# Revit family: Reece_Tap_Mizu_Bloc_Bath Outlet_160 mm
name_source: partatom
category: Plumbing Fixtures
revit_build: Autodesk Revit 2018 (Build: 20190510_1515(x64)
units: mm (PartAtom-declared; Revit-internal decimal feet)

## family parameters
Cut with Voids When Loaded = No
Host = Face
Part Type = Normal
Room Calculation Point = Yes
Round Connector Dimension = Use Diameter
Shared = Yes

## types (1)
- Chrome
    CWFU = 0
    Default Elevation = 1000 mm  [stored 3.28084 ft]
    Description = Mizu Bloc Bath Outlet 160mm Chrome
    Disclaimer = THIS FILE IS THE PROPERTY OF THE REECE GROUP. IT MAY NOT BE REPRODUCED, REVERSE-ENGINEERED OR MODIFIED. ANY REPUBLICATION, TRANSMISSION OR DISTRIBUTION FOR THE PURPOSE OF COMMERCIALLY EXPLOITING THE FILES IS PROHIBITED.
    HWFU = 0
    Keynote = Product #9503476, Reece_Tap_Mizu_Bloc_Bath Outlet_160 mm - Chrome
    Manufacturer = Mizu
    Model = Bloc
    Reece_Detail_Additional = Bath Outlet
    Reece_Detail_Disclaimer = THIS FILE IS THE PROPERTY OF THE REECE GROUP. IT MAY NOT BE REPRODUCED, REVERSE-ENGINEERED OR MODIFIED. ANY REPUBLICATION, TRANSMISSION OR DISTRIBUTION FOR THE PURPOSE OF COMMERCIALLY EXPLOITING THE FILES IS PROHIBITED.
    Reece_Material-Main = Reece_Brass_Chrome
    Reece_Overall_Width = 61 mm  [stored 0.200131 ft]
    Reece_Product_Brand = Mizu
    Reece_Product_Description = Mizu Bloc Bath Outlet 160mm Chrome
    Reece_Product_Mount = Wall Mounted
    Reece_Product_Number = 9503476
    Reece_Product_Sub Brand = Bloc
    Reece_Product_Type = Tap
    Reece_Product_Web Page = https://www.reece.com.au
    Reece_Tap_Inlet = 13 mm
    Reece_Tap_Reach = 160 mm  [stored 0.524934 ft]
    Type Comments = Tap
    URL = https://www.reece.com.au
    WFU = 0

note: [stored X ft] marks values corroborated as IEEE doubles in the binary element streams (Revit-internal decimal feet)

## geometry (parser evidence)
native form markers: Sweep x1
no freeform markers — native parametric forms only
